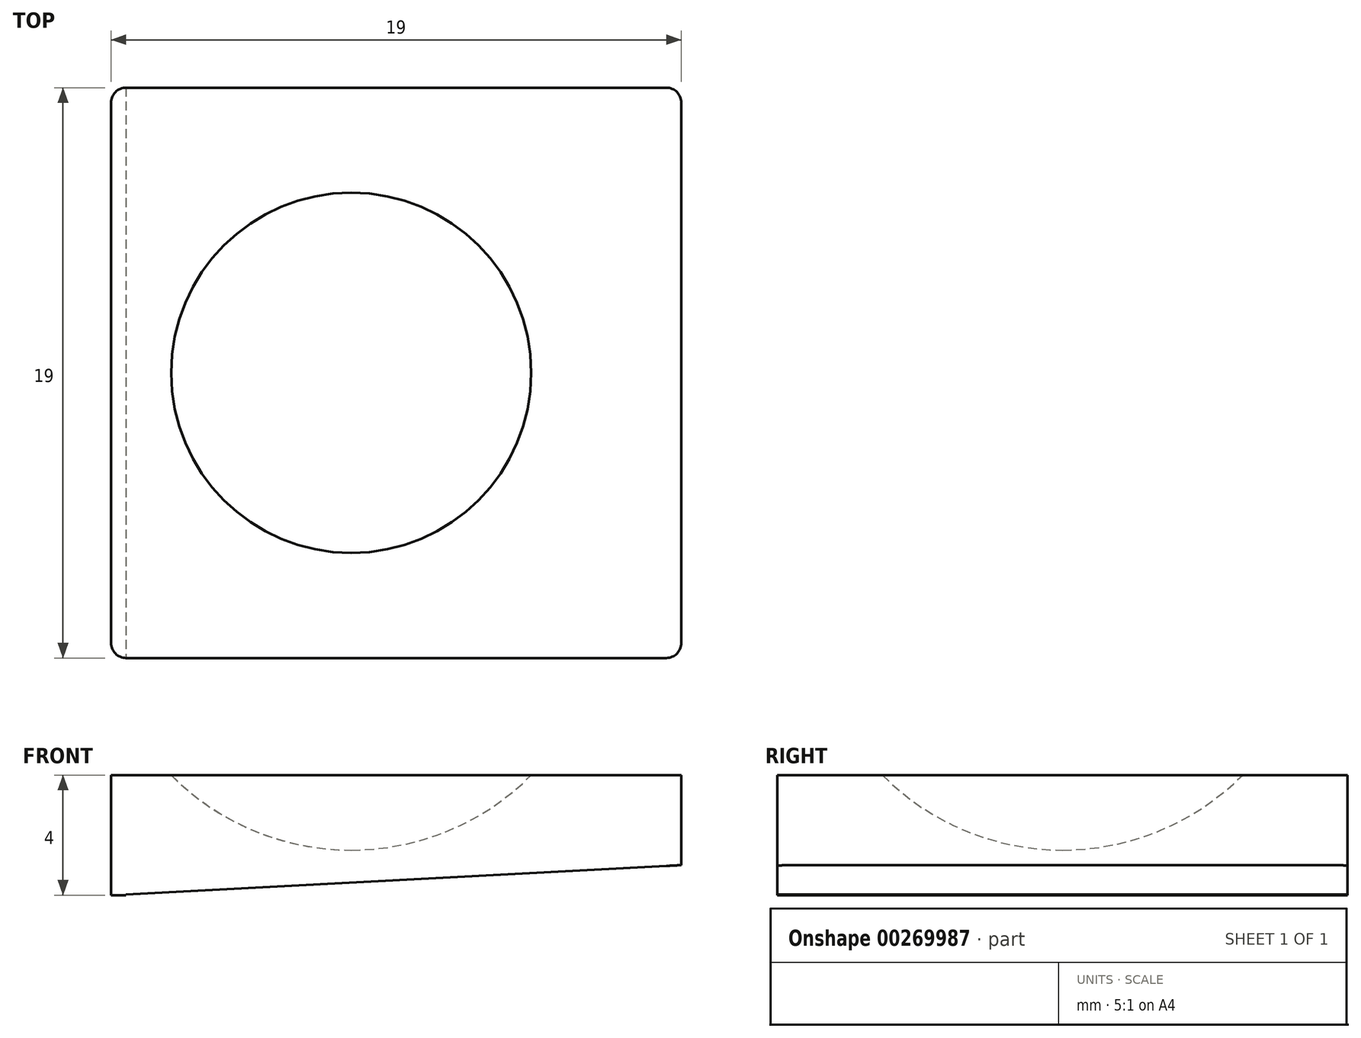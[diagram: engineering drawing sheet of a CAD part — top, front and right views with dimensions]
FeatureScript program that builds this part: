
annotation { "Feature Type Name" : "Feature", "Feature Type Description" : "" }
export const myFeature = defineFeature(function(context is Context, id is Id, definition is map)
    precondition{}
    {
        {
            var Q0;
            Q0=qCreatedBy(makeId("Top.planeOp"),FACE);
            var sketch = newSketch(context, id + "F0", { "sketchPlane" : qUnion([Q0])});
            skLineSegment(sketch, "E0.bottom", {"start": v(9, 9.5) * mm, "end": v(-9, 9.5) * mm});
            skLineSegment(sketch, "E0.top", {"start": v(9, -9.5) * mm, "end": v(-9, -9.5) * mm});
            skLineSegment(sketch, "E0.left", {"start": v(9.5, 9) * mm, "end": v(9.5, -9) * mm});
            skLineSegment(sketch, "E0.right", {"start": v(-9.5, 9) * mm, "end": v(-9.5, -9) * mm});
            skPoint(sketch, "E0.middle", {"position": v(0, 0) * mm});
            skPoint(sketch, "E1.visualSharp", {"position": v(-9.5, 9.5) * mm});
            skArc(sketch, "E1.filletArc", {"start": v(-9, 9.5) * mm, "mid": v(-9.35, 9.35) * mm, "end": v(-9.5, 9) * mm});
            skArc(sketch, "E2.MirrorCS", {"start": v(9, 9.5) * mm, "mid": v(9.35, 9.35) * mm, "end": v(9.5, 9) * mm});
            skArc(sketch, "E3.MirrorCS", {"start": v(9, -9.5) * mm, "mid": v(9.35, -9.35) * mm, "end": v(9.5, -9) * mm});
            skArc(sketch, "E4.MirrorCS", {"start": v(-9, -9.5) * mm, "mid": v(-9.35, -9.35) * mm, "end": v(-9.5, -9) * mm});
            skPoint(sketch, "E5.orphan", {"position": v(9.5, 9.5) * mm});
            skPoint(sketch, "E6.orphan", {"position": v(9.5, -9.5) * mm});
            skPoint(sketch, "E7.orphan", {"position": v(-9.5, -9.5) * mm});
            skSolve(sketch);
        }
        {
            var Q0;
            Q0=makeQuery(id+"F0.imprint","IMPRINT",FACE,{"disambiguationData":[TD([[makeQuery(id+"F0.imprint","IMPRINT",EDGE,{"derivedFrom":sQuery(id+"F0.wireOp",EDGE,"E0.bottom")}),1.0]])]});
            extrude(context, id + "F1", {"entities" : qUnion([Q0]), "depth" : 4 * mm, "offsetDistance" : 25 * mm});
        }
        {
            var Q0;
            Q0=makeQuery(id+"F1.opExtrude","SWEPT_FACE",FACE,{"disambiguationData":[OSD([sQuery(id+"F0.wireOp",EDGE,"E0.top")])]});
            var sketch = newSketch(context, id + "F2", { "sketchPlane" : qUnion([Q0])});
            skLineSegment(sketch, "E8", {"start": v(-9.5, 0) * mm, "end": v(9.5, 1) * mm});
            skLineSegment(sketch, "E9", {"start": v(9.5, 1) * mm, "end": v(9.5, 0) * mm});
            skLineSegment(sketch, "E10", {"start": v(9.5, 0) * mm, "end": v(-9.5, 0) * mm});
            skSolve(sketch);
        }
        {
            var Q0;
            {var subQ0=sQuery(id+"F2.wireOp",EDGE,"E8");var subQ1=sQuery(id+"F0.wireOp",EDGE,"E0.top");var subQ2=makeQuery(id+"F1.opExtrude","SWEPT_EDGE",EDGE,{"disambiguationData":[OSD([subQ1,sQuery(id+"F0.wireOp",EDGE,"E4.MirrorCS")])]});var subQ3=makeQuery(id+"F2.imprint","INTERSECT",VERTEX,{"derivedFrom":[subQ2,subQ0]});Q0=makeQuery(id+"F2.imprint","IMPRINT",FACE,{"disambiguationData":[TD([[makeQuery(id+"F2.imprint","IMPRINT",EDGE,{"disambiguationData":[TD([[subQ3,-1.0]])],"derivedFrom":subQ0}),-1.0]])]});}
            var Q1;
            {var subQ0=sQuery(id+"F2.wireOp",EDGE,"E9");Q1=makeQuery(id+"F2.imprint","IMPRINT",FACE,{"disambiguationData":[TD([[makeQuery(id+"F2.imprint","IMPRINT",EDGE,{"derivedFrom":subQ0}),-1.0]])]});}
            var Q2;
            Q2=makeQuery(id+"F1.opExtrude","SWEPT_FACE",FACE,{"disambiguationData":[OSD([sQuery(id+"F0.wireOp",EDGE,"E0.bottom")])]});
            extrude(context, id + "F3", {"entities" : qUnion([Q0, Q1]), "operationType" : NewBodyOperationType.REMOVE, "endBound" : BoundingType.UP_TO_SURFACE, "oppositeDirection" : true, "depth" : 25 * mm, "endBoundEntityFace" : qUnion([Q2]), "offsetDistance" : 25 * mm});
        }
        {
            var Q0;
            Q0=qCreatedBy(makeId("Front.planeOp"),FACE);
            var sketch = newSketch(context, id + "F4", { "sketchPlane" : qUnion([Q0])});
            skLineSegment(sketch, "E11", {"start": v(-1.5, 9.3) * mm, "end": v(-1.5, -4.58) * mm, "construction": true});
            skPoint(sketch, "E12", {"position": v(-7.5, 4) * mm});
            skPoint(sketch, "E13", {"position": v(-1.5, 1.5) * mm});
            skLineSegment(sketch, "E14", {"start": v(-2.76, 4) * mm, "end": v(-0.24, 4) * mm, "construction": true});
            skPoint(sketch, "E15", {"position": v(-1.5, 4) * mm});
            skPoint(sketch, "E16.MirrorP", {"position": v(4.5, 4) * mm});
            skArc(sketch, "E17", {"start": v(-7.5, 4) * mm, "mid": v(-4.75, 2.15) * mm, "end": v(-1.5, 1.5) * mm});
            skLineSegment(sketch, "E18", {"start": v(-7.5, 4) * mm, "end": v(-1.5, 4) * mm});
            skLineSegment(sketch, "E19", {"start": v(-1.5, 4) * mm, "end": v(-1.5, 1.5) * mm});
            skSolve(sketch);
        }
        {
            var Q0;
            Q0=makeQuery(id+"F4.imprint","IMPRINT",FACE,{"disambiguationData":[TD([[makeQuery(id+"F4.imprint","IMPRINT",EDGE,{"derivedFrom":sQuery(id+"F4.wireOp",EDGE,"E17")}),1.0]])]});
            var Q1;
            Q1=sQuery(id+"F4.wireOp",EDGE,"E11");
            revolve(context, id + "F5", {"operationType" : NewBodyOperationType.REMOVE, "surfaceOperationType" : NewSurfaceOperationType.NEW, "entities" : qUnion([Q0]), "axis" : qUnion([Q1]), "revolveType" : RevolveType.FULL, "oppositeDirection" : true});
        }
    });
